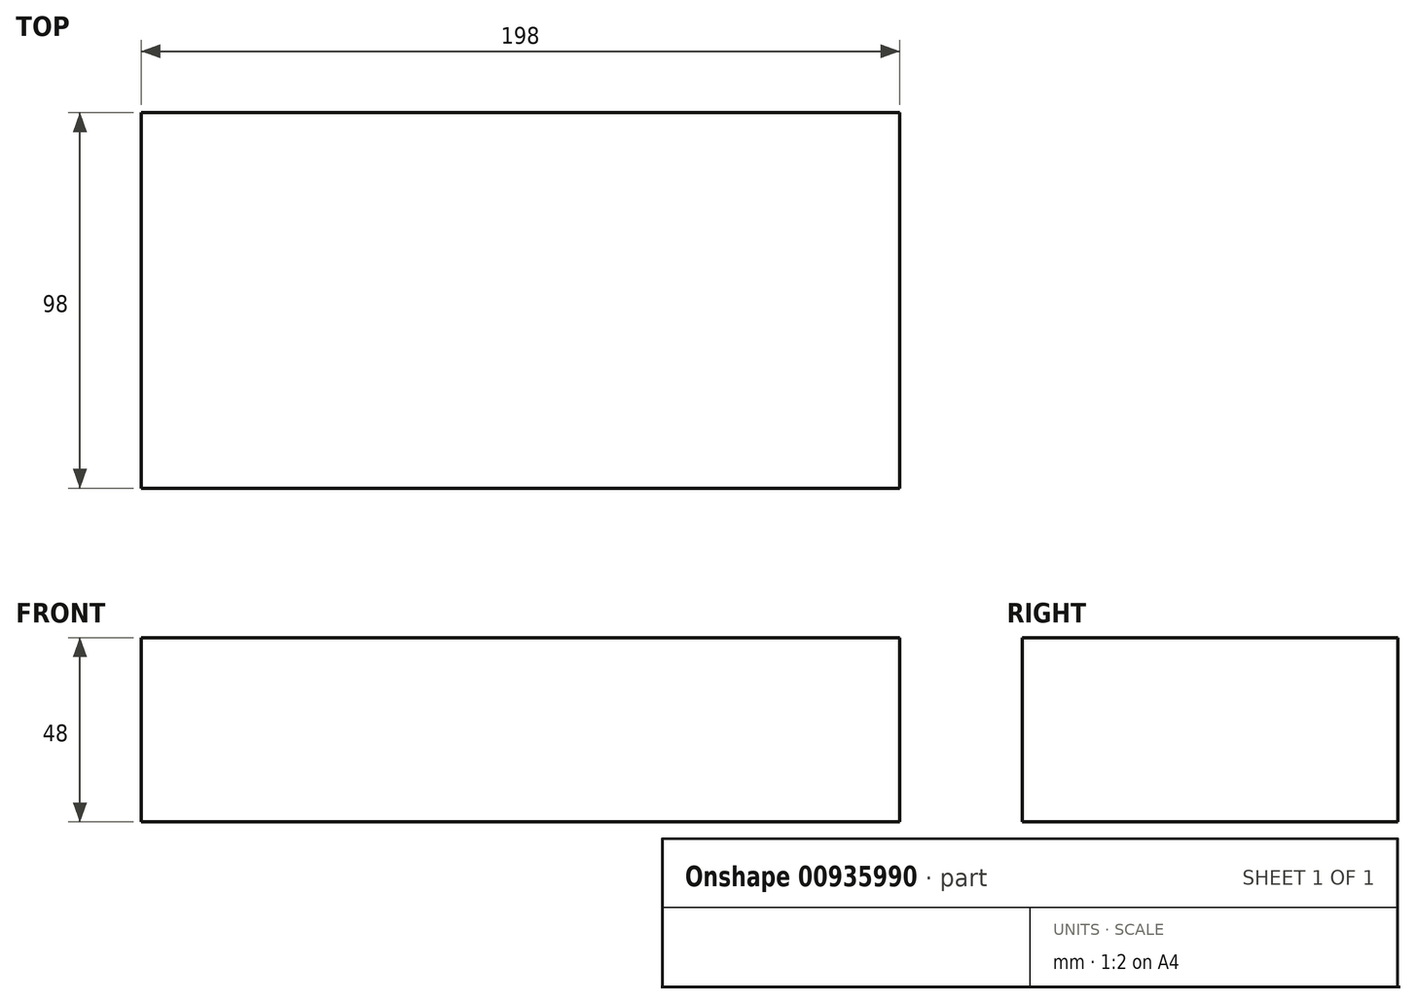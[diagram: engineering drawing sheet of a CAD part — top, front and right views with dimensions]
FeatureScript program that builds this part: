
annotation { "Feature Type Name" : "Feature", "Feature Type Description" : "" }
export const myFeature = defineFeature(function(context is Context, id is Id, definition is map)
    precondition{}
    {
        {
            var Q0;
            Q0=qCreatedBy(makeId("Right.planeOp"),FACE);
            var sketch = newSketch(context, id + "F0", { "sketchPlane" : qUnion([Q0])});
            skLineSegment(sketch, "E0.bottom", {"start": v(49, -24) * mm, "end": v(-49, -24) * mm});
            skLineSegment(sketch, "E0.top", {"start": v(49, 24) * mm, "end": v(-49, 24) * mm});
            skLineSegment(sketch, "E0.left", {"start": v(49, -24) * mm, "end": v(49, 24) * mm});
            skLineSegment(sketch, "E0.right", {"start": v(-49, -24) * mm, "end": v(-49, 24) * mm});
            skPoint(sketch, "E0.middle", {"position": v(0, 0) * mm});
            skSolve(sketch);
        }
        {
            assignVariable(context, id + "F1", {"name" : "Length", "anyValue" : 198});
        }
        {
            var Q0;
            Q0=qSketchRegion(id+"F0",true);
            extrude(context, id + "F2", {"entities" : qUnion([Q0]), "depth" : (getVariable(context, 'Length')) * mm, "offsetDistance" : 25 * mm});
        }
    });
